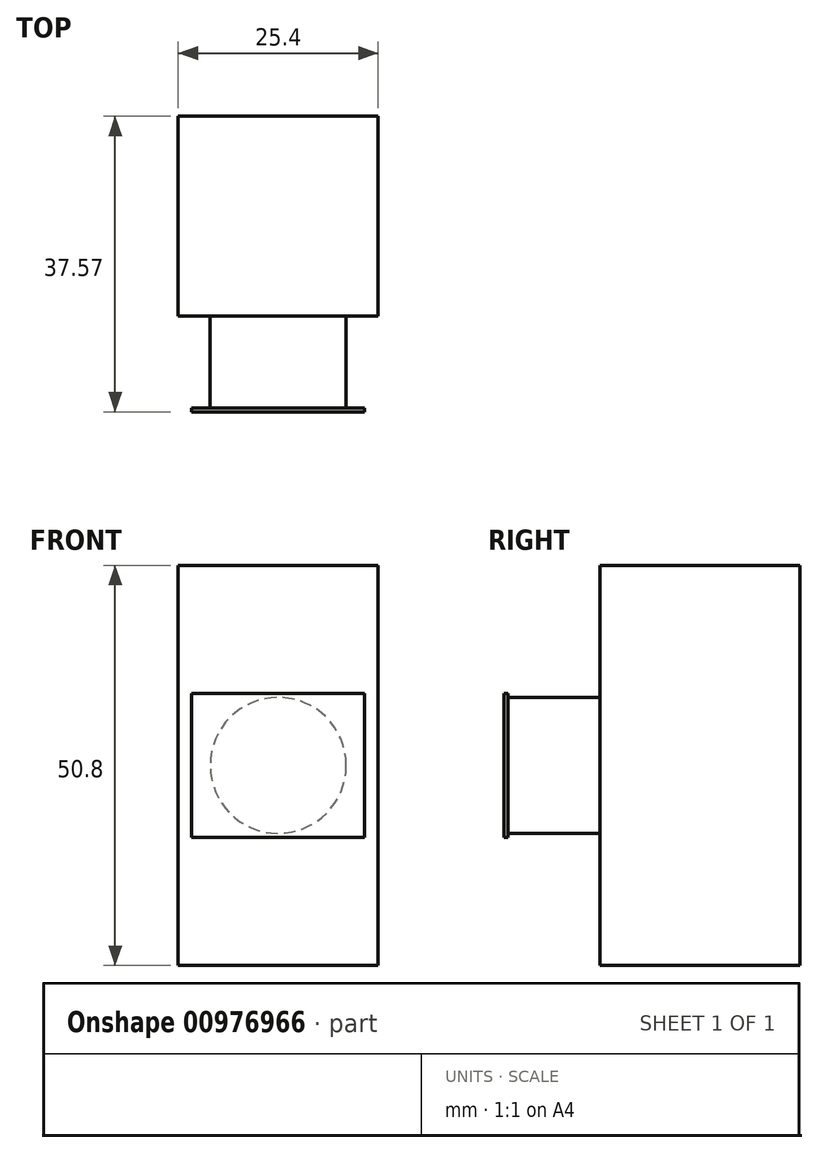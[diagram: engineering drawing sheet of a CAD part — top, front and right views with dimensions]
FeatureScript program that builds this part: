
annotation { "Feature Type Name" : "Feature", "Feature Type Description" : "" }
export const myFeature = defineFeature(function(context is Context, id is Id, definition is map)
    precondition{}
    {
        {
            var Q0;
            Q0=qCreatedBy(makeId("Front.planeOp"),FACE);
            var sketch = newSketch(context, id + "F0", { "sketchPlane" : qUnion([Q0])});
            skLineSegment(sketch, "E0.bottom", {"start": v(12.7, 25.4) * mm, "end": v(-12.7, 25.4) * mm});
            skLineSegment(sketch, "E0.top", {"start": v(12.7, -25.4) * mm, "end": v(-12.7, -25.4) * mm});
            skLineSegment(sketch, "E0.left", {"start": v(12.7, 25.4) * mm, "end": v(12.7, -25.4) * mm});
            skLineSegment(sketch, "E0.right", {"start": v(-12.7, 25.4) * mm, "end": v(-12.7, -25.4) * mm});
            skPoint(sketch, "E0.middle", {"position": v(0, 0) * mm});
            skSolve(sketch);
        }
        {
            var Q0;
            Q0 = qSketchRegion(id + "F0", true);
            extrude(context, id + "F1", {"entities" : qUnion([Q0]), "depth" : 25.4 * mm, "offsetDistance" : 25.4 * mm});
        }
        {
            var Q0;
            Q0=makeQuery(id+"F1.opExtrude","CAP_FACE",FACE,{"disambiguationData":[OSD([sQuery(id+"F0.wireOp",EDGE,"E0.bottom"),sQuery(id+"F0.wireOp",EDGE,"E0.top"),sQuery(id+"F0.wireOp",EDGE,"E0.left"),sQuery(id+"F0.wireOp",EDGE,"E0.right")])],"isStart":false});
            var sketch = newSketch(context, id + "F2", { "sketchPlane" : qUnion([Q0])});
            skCircle(sketch, "E1", {"center": v(0, 0) * mm, "radius": 8.64 * mm});
            skSolve(sketch);
        }
        {
            var Q0;
            Q0 = qSketchRegion(id + "F2", true);
            extrude(context, id + "F3", {"entities" : qUnion([Q0]), "operationType" : NewBodyOperationType.REMOVE, "oppositeDirection" : true, "depth" : 24.64 * mm, "offsetDistance" : 25.4 * mm});
        }
        {
            var Q0;
            Q0=makeQuery(id+"F3.boolean.opBoolean","COPY",FACE,{"derivedFrom":makeQuery(id+"F3.opExtrude","CAP_FACE",FACE,{"disambiguationData":[OSD([sQuery(id+"F2.wireOp",EDGE,"E1")])],"isStart":false})});
            extrude(context, id + "F4", {"entities" : qUnion([Q0]), "operationType" : NewBodyOperationType.ADD, "depth" : 36.32 * mm, "offsetDistance" : 25.4 * mm});
        }
        {
            var Q0;
            Q0=makeQuery(id+"F4.opExtrude","CAP_FACE",FACE,{"disambiguationData":[OSD([sQuery(id+"F2.wireOp",EDGE,"E1")])],"isStart":false});
            var sketch = newSketch(context, id + "F5", { "sketchPlane" : qUnion([Q0])});
            skPoint(sketch, "E2", {"position": v(0, 0) * mm});
            skLineSegment(sketch, "E3.bottom", {"start": v(10.98, 9.17) * mm, "end": v(-10.98, 9.17) * mm});
            skLineSegment(sketch, "E3.top", {"start": v(10.98, -9.17) * mm, "end": v(-10.98, -9.17) * mm});
            skLineSegment(sketch, "E3.left", {"start": v(10.98, 9.17) * mm, "end": v(10.98, -9.17) * mm});
            skLineSegment(sketch, "E3.right", {"start": v(-10.98, 9.17) * mm, "end": v(-10.98, -9.17) * mm});
            skSolve(sketch);
        }
        {
            var Q0;
            Q0 = qSketchRegion(id + "F5", true);
            extrude(context, id + "F6", {"entities" : qUnion([Q0]), "operationType" : NewBodyOperationType.ADD, "depth" : 0.48 * mm, "offsetDistance" : 25.4 * mm});
        }
    });
